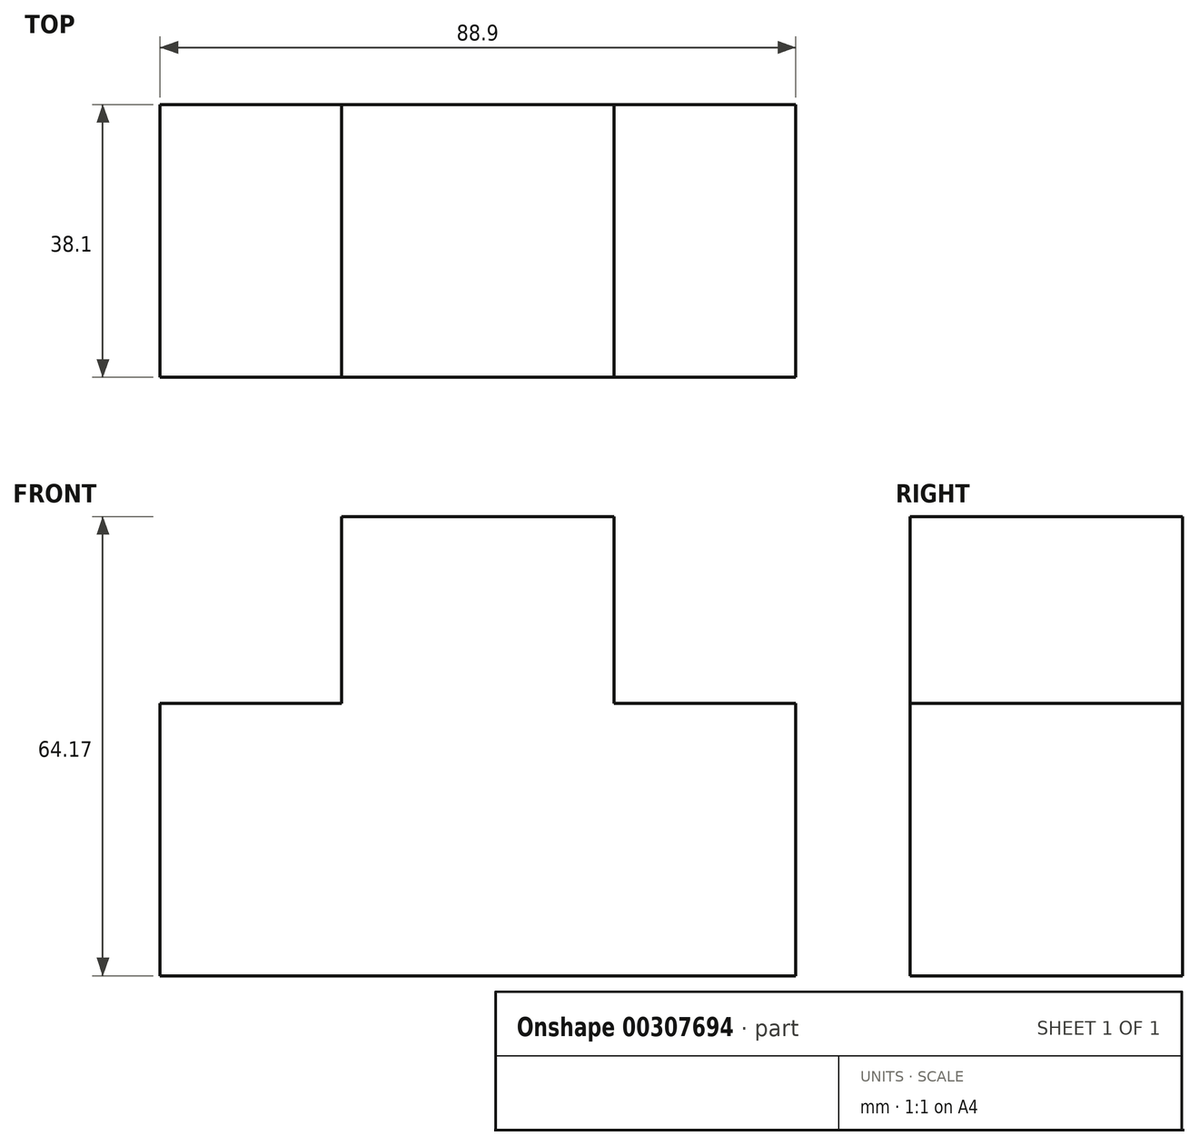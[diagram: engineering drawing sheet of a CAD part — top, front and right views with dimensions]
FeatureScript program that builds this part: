
annotation { "Feature Type Name" : "Feature", "Feature Type Description" : "" }
export const myFeature = defineFeature(function(context is Context, id is Id, definition is map)
    precondition{}
    {
        {
            var Q0;
            Q0=qCreatedBy(makeId("Front.planeOp"),FACE);
            var sketch = newSketch(context, id + "F0", { "sketchPlane" : qUnion([Q0])});
            skLineSegment(sketch, "E0", {"start": v(-47.92, -41.32) * mm, "end": v(40.98, -41.32) * mm});
            skLineSegment(sketch, "E1", {"start": v(40.98, -41.32) * mm, "end": v(40.98, -3.22) * mm});
            skLineSegment(sketch, "E2", {"start": v(40.98, -3.22) * mm, "end": v(15.58, -3.22) * mm});
            skLineSegment(sketch, "E3", {"start": v(15.58, -3.22) * mm, "end": v(15.58, 22.85) * mm});
            skLineSegment(sketch, "E4", {"start": v(15.58, 22.85) * mm, "end": v(-22.52, 22.85) * mm});
            skLineSegment(sketch, "E5", {"start": v(-22.52, 22.85) * mm, "end": v(-22.52, -3.22) * mm});
            skLineSegment(sketch, "E6", {"start": v(-22.52, -3.22) * mm, "end": v(-47.92, -3.22) * mm});
            skLineSegment(sketch, "E7", {"start": v(-47.92, -3.22) * mm, "end": v(-47.92, -41.32) * mm});
            skSolve(sketch);
        }
        {
            var Q0;
            Q0=makeQuery(id+"F0.imprint","IMPRINT",FACE,{"disambiguationData":[TD([[makeQuery(id+"F0.imprint","IMPRINT",EDGE,{"derivedFrom":sQuery(id+"F0.wireOp",EDGE,"E0")}),1.0]])]});
            extrude(context, id + "F1", {"entities" : qUnion([Q0]), "depth" : 38.1 * mm});
        }
    });
